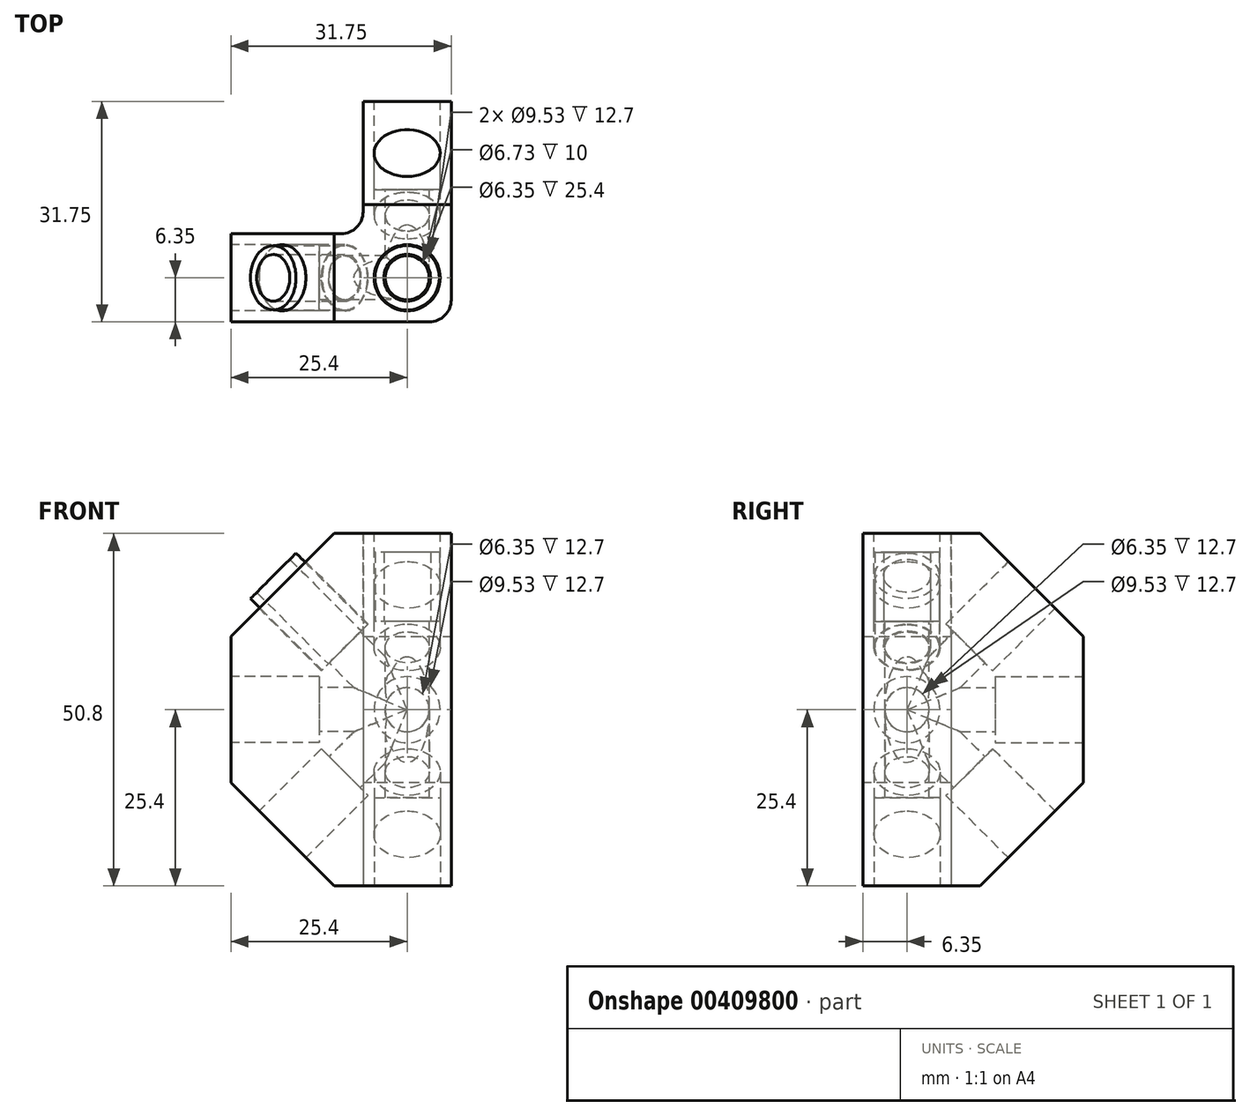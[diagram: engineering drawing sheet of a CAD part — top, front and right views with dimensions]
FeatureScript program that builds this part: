
annotation { "Feature Type Name" : "Feature", "Feature Type Description" : "" }
export const myFeature = defineFeature(function(context is Context, id is Id, definition is map)
    precondition{}
    {
        {
            var Q0;
            Q0=qCreatedBy(makeId("Top.planeOp"),FACE);
            var sketch = newSketch(context, id + "F0", { "sketchPlane" : qUnion([Q0])});
            skLineSegment(sketch, "E0.bottom", {"start": v(-6.35, 6.35) * mm, "end": v(-25.4, 6.35) * mm});
            skLineSegment(sketch, "E0.top", {"start": v(6.35, -6.35) * mm, "end": v(-25.4, -6.35) * mm});
            skLineSegment(sketch, "E0.right", {"start": v(-25.4, 6.35) * mm, "end": v(-25.4, -6.35) * mm});
            skLineSegment(sketch, "E1.top", {"start": v(-6.35, 25.4) * mm, "end": v(6.35, 25.4) * mm});
            skLineSegment(sketch, "E1.left", {"start": v(-6.35, 6.35) * mm, "end": v(-6.35, 25.4) * mm});
            skLineSegment(sketch, "E1.right", {"start": v(6.35, -6.35) * mm, "end": v(6.35, 25.4) * mm});
            skSolve(sketch);
        }
        {
            var Q0;
            Q0 = qSketchRegion(id + "F0", true);
            extrude(context, id + "F1", {"entities" : qUnion([Q0]), "depth" : 50.8 * mm, "symmetric" : true});
        }
        {
            var Q0;
            Q0=makeQuery(id+"F1.opExtrude","CAP_EDGE",EDGE,{"disambiguationData":[OSD([sQuery(id+"F0.wireOp",EDGE,"E0.right")])],"isStart":false});
            var Q1;
            Q1=makeQuery(id+"F1.opExtrude","CAP_EDGE",EDGE,{"disambiguationData":[OSD([sQuery(id+"F0.wireOp",EDGE,"E0.right")])],"isStart":true});
            var Q2;
            Q2=makeQuery(id+"F1.opExtrude","CAP_EDGE",EDGE,{"disambiguationData":[OSD([sQuery(id+"F0.wireOp",EDGE,"E1.top")])],"isStart":true});
            var Q3;
            Q3=makeQuery(id+"F1.opExtrude","CAP_EDGE",EDGE,{"disambiguationData":[OSD([sQuery(id+"F0.wireOp",EDGE,"E1.top")])],"isStart":false});
            chamfer(context, id + "F2", {"entities" : qUnion([Q0, Q1, Q2, Q3]), "width" : 14.86 * mm, "tangentPropagation" : true});
        }
        {
            var Q0;
            Q0=makeQuery(id+"F1.opExtrude","CAP_FACE",FACE,{"disambiguationData":[OSD([sQuery(id+"F0.wireOp",EDGE,"E0.bottom"),sQuery(id+"F0.wireOp",EDGE,"E0.top"),sQuery(id+"F0.wireOp",EDGE,"E0.right"),sQuery(id+"F0.wireOp",EDGE,"E1.top"),sQuery(id+"F0.wireOp",EDGE,"E1.left"),sQuery(id+"F0.wireOp",EDGE,"E1.right")])],"isStart":false});
            var sketch = newSketch(context, id + "F3", { "sketchPlane" : qUnion([Q0])});
            skCircle(sketch, "E2", {"center": v(0, 0) * mm, "radius": 3.18 * mm});
            skSolve(sketch);
        }
        {
            var Q0;
            Q0 = qSketchRegion(id + "F3", true);
            extrude(context, id + "F4", {"entities" : qUnion([Q0]), "operationType" : NewBodyOperationType.REMOVE, "endBound" : BoundingType.THROUGH_ALL, "oppositeDirection" : true, "depth" : 25.4 * mm});
        }
        {
            var Q0;
            Q0=makeQuery(id+"F1.opExtrude","SWEPT_FACE",FACE,{"disambiguationData":[OSD([sQuery(id+"F0.wireOp",EDGE,"E0.right")])]});
            var sketch = newSketch(context, id + "F5", { "sketchPlane" : qUnion([Q0])});
            skCircle(sketch, "E3", {"center": v(0, 0) * mm, "radius": 3.18 * mm});
            skSolve(sketch);
        }
        {
            var Q0;
            Q0 = qSketchRegion(id + "F5", true);
            extrude(context, id + "F6", {"entities" : qUnion([Q0]), "operationType" : NewBodyOperationType.REMOVE, "endBound" : BoundingType.UP_TO_NEXT, "oppositeDirection" : true, "depth" : 25.4 * mm});
        }
        {
            var Q0;
            Q0=makeQuery(id+"F1.opExtrude","SWEPT_FACE",FACE,{"disambiguationData":[OSD([sQuery(id+"F0.wireOp",EDGE,"E1.top")])]});
            var sketch = newSketch(context, id + "F7", { "sketchPlane" : qUnion([Q0])});
            skCircle(sketch, "E4", {"center": v(0, 0) * mm, "radius": 3.18 * mm});
            skSolve(sketch);
        }
        {
            var Q0;
            Q0 = qSketchRegion(id + "F7", true);
            extrude(context, id + "F8", {"entities" : qUnion([Q0]), "operationType" : NewBodyOperationType.REMOVE, "endBound" : BoundingType.UP_TO_NEXT, "oppositeDirection" : true, "depth" : 25.4 * mm});
        }
        {
            var Q0;
            {var subQ0=sQuery(id+"F0.wireOp",EDGE,"E1.top");Q0=makeQuery(id+"F2.opChamfer","BLEND_FACE",FACE,{"disambiguationData":[OSD([subQ0]),TDD([makeQuery(id+"F1.opExtrude","CAP_EDGE",EDGE,{"disambiguationData":[OSD([subQ0])],"isStart":false})])]});}
            var sketch = newSketch(context, id + "F9", { "sketchPlane" : qUnion([Q0])});
            skCircle(sketch, "E5", {"center": v(0, 0) * mm, "radius": 3.18 * mm});
            skSolve(sketch);
        }
        {
            var Q0;
            Q0 = qSketchRegion(id + "F9", true);
            extrude(context, id + "F10", {"entities" : qUnion([Q0]), "operationType" : NewBodyOperationType.REMOVE, "endBound" : BoundingType.UP_TO_NEXT, "oppositeDirection" : true, "depth" : 25.4 * mm});
        }
        {
            var Q0;
            {var subQ0=sQuery(id+"F0.wireOp",EDGE,"E0.right");Q0=makeQuery(id+"F2.opChamfer","BLEND_FACE",FACE,{"disambiguationData":[OSD([subQ0]),TDD([makeQuery(id+"F1.opExtrude","CAP_EDGE",EDGE,{"disambiguationData":[OSD([subQ0])],"isStart":false})])]});}
            var sketch = newSketch(context, id + "F11", { "sketchPlane" : qUnion([Q0])});
            skCircle(sketch, "E6", {"center": v(0, 0) * mm, "radius": 3.18 * mm});
            skSolve(sketch);
        }
        {
            var Q0;
            Q0 = qSketchRegion(id + "F11", true);
            extrude(context, id + "F12", {"entities" : qUnion([Q0]), "operationType" : NewBodyOperationType.REMOVE, "endBound" : BoundingType.UP_TO_NEXT, "oppositeDirection" : true, "depth" : 25.4 * mm});
        }
        {
            var Q0;
            {var subQ0=sQuery(id+"F0.wireOp",EDGE,"E1.top");Q0=makeQuery(id+"F2.opChamfer","BLEND_FACE",FACE,{"disambiguationData":[OSD([subQ0]),TDD([makeQuery(id+"F1.opExtrude","CAP_EDGE",EDGE,{"disambiguationData":[OSD([subQ0])],"isStart":true})])]});}
            var sketch = newSketch(context, id + "F13", { "sketchPlane" : qUnion([Q0])});
            skCircle(sketch, "E7", {"center": v(0, 0) * mm, "radius": 3.18 * mm});
            skSolve(sketch);
        }
        {
            var Q0;
            Q0 = qSketchRegion(id + "F13", true);
            extrude(context, id + "F14", {"entities" : qUnion([Q0]), "operationType" : NewBodyOperationType.REMOVE, "endBound" : BoundingType.UP_TO_NEXT, "oppositeDirection" : true, "depth" : 25.4 * mm});
        }
        {
            var Q0;
            {var subQ0=sQuery(id+"F0.wireOp",EDGE,"E0.right");Q0=makeQuery(id+"F2.opChamfer","BLEND_FACE",FACE,{"disambiguationData":[OSD([subQ0]),TDD([makeQuery(id+"F1.opExtrude","CAP_EDGE",EDGE,{"disambiguationData":[OSD([subQ0])],"isStart":true})])]});}
            var sketch = newSketch(context, id + "F15", { "sketchPlane" : qUnion([Q0])});
            skCircle(sketch, "E8", {"center": v(0, 0) * mm, "radius": 3.18 * mm});
            skSolve(sketch);
        }
        {
            var Q0;
            Q0 = qSketchRegion(id + "F15", true);
            extrude(context, id + "F16", {"entities" : qUnion([Q0]), "operationType" : NewBodyOperationType.REMOVE, "endBound" : BoundingType.UP_TO_NEXT, "oppositeDirection" : true, "depth" : 25.4 * mm});
        }
        {
            var Q0;
            Q0=makeQuery(id+"F1.opExtrude","SWEPT_EDGE",EDGE,{"disambiguationData":[OSD([sQuery(id+"F0.wireOp",EDGE,"E0.bottom"),sQuery(id+"F0.wireOp",EDGE,"E1.left")])]});
            fillet(context, id + "F17", {"entities" : qUnion([Q0]), "radius" : 3.17 * mm, "tangentPropagation" : true, "allowEdgeOverflow" : false});
        }
        {
            var Q0;
            Q0=makeQuery(id+"F1.opExtrude","SWEPT_EDGE",EDGE,{"disambiguationData":[OSD([sQuery(id+"F0.wireOp",EDGE,"E0.top"),sQuery(id+"F0.wireOp",EDGE,"E1.right")])]});
            fillet(context, id + "F18", {"entities" : qUnion([Q0]), "radius" : 3.17 * mm, "tangentPropagation" : true, "allowEdgeOverflow" : false});
        }
        {
            var Q0;
            Q0=makeQuery(id+"F1.opExtrude","CAP_FACE",FACE,{"disambiguationData":[OSD([sQuery(id+"F0.wireOp",EDGE,"E0.bottom"),sQuery(id+"F0.wireOp",EDGE,"E0.top"),sQuery(id+"F0.wireOp",EDGE,"E0.right"),sQuery(id+"F0.wireOp",EDGE,"E1.top"),sQuery(id+"F0.wireOp",EDGE,"E1.left"),sQuery(id+"F0.wireOp",EDGE,"E1.right")])],"isStart":true});
            var sketch = newSketch(context, id + "F19", { "sketchPlane" : qUnion([Q0])});
            skCircle(sketch, "E9", {"center": v(0, 0) * mm, "radius": 4.76 * mm});
            skSolve(sketch);
        }
        {
            var Q0;
            Q0 = qSketchRegion(id + "F19", true);
            extrude(context, id + "F20", {"entities" : qUnion([Q0]), "operationType" : NewBodyOperationType.REMOVE, "oppositeDirection" : true, "depth" : 12.7 * mm});
        }
        {
            var Q0;
            Q0=makeQuery(id+"F1.opExtrude","CAP_FACE",FACE,{"disambiguationData":[OSD([sQuery(id+"F0.wireOp",EDGE,"E0.bottom"),sQuery(id+"F0.wireOp",EDGE,"E0.top"),sQuery(id+"F0.wireOp",EDGE,"E0.right"),sQuery(id+"F0.wireOp",EDGE,"E1.top"),sQuery(id+"F0.wireOp",EDGE,"E1.left"),sQuery(id+"F0.wireOp",EDGE,"E1.right")])],"isStart":false});
            var sketch = newSketch(context, id + "F21", { "sketchPlane" : qUnion([Q0])});
            skCircle(sketch, "E10", {"center": v(0, 0) * mm, "radius": 4.76 * mm});
            skSolve(sketch);
        }
        {
            var Q0;
            Q0 = qSketchRegion(id + "F21", true);
            extrude(context, id + "F22", {"entities" : qUnion([Q0]), "operationType" : NewBodyOperationType.REMOVE, "oppositeDirection" : true, "depth" : 12.7 * mm});
        }
        {
            var Q0;
            Q0=makeQuery(id+"F1.opExtrude","SWEPT_FACE",FACE,{"disambiguationData":[OSD([sQuery(id+"F0.wireOp",EDGE,"E0.right")])]});
            var sketch = newSketch(context, id + "F23", { "sketchPlane" : qUnion([Q0])});
            skCircle(sketch, "E11", {"center": v(0, 0) * mm, "radius": 4.76 * mm});
            skSolve(sketch);
        }
        {
            var Q0;
            Q0 = qSketchRegion(id + "F23", true);
            extrude(context, id + "F24", {"entities" : qUnion([Q0]), "operationType" : NewBodyOperationType.REMOVE, "oppositeDirection" : true, "depth" : 12.7 * mm});
        }
        {
            var Q0;
            Q0=makeQuery(id+"F1.opExtrude","SWEPT_FACE",FACE,{"disambiguationData":[OSD([sQuery(id+"F0.wireOp",EDGE,"E1.top")])]});
            var sketch = newSketch(context, id + "F25", { "sketchPlane" : qUnion([Q0])});
            skCircle(sketch, "E12", {"center": v(0, 0) * mm, "radius": 4.76 * mm});
            skSolve(sketch);
        }
        {
            var Q0;
            Q0 = qSketchRegion(id + "F25", true);
            extrude(context, id + "F26", {"entities" : qUnion([Q0]), "operationType" : NewBodyOperationType.REMOVE, "oppositeDirection" : true, "depth" : 12.7 * mm});
        }
        {
            var Q0;
            {var subQ0=sQuery(id+"F0.wireOp",EDGE,"E0.right");Q0=makeQuery(id+"F2.opChamfer","BLEND_FACE",FACE,{"disambiguationData":[OSD([subQ0]),TDD([makeQuery(id+"F1.opExtrude","CAP_EDGE",EDGE,{"disambiguationData":[OSD([subQ0])],"isStart":false})])]});}
            var sketch = newSketch(context, id + "F27", { "sketchPlane" : qUnion([Q0])});
            skCircle(sketch, "E13", {"center": v(0, 0) * mm, "radius": 4.76 * mm});
            skSolve(sketch);
        }
        {
            var Q0;
            Q0 = qSketchRegion(id + "F27", true);
            extrude(context, id + "F28", {"entities" : qUnion([Q0]), "operationType" : NewBodyOperationType.REMOVE, "oppositeDirection" : true, "depth" : 12.7 * mm});
        }
        {
            var Q0;
            {var subQ0=sQuery(id+"F0.wireOp",EDGE,"E1.top");Q0=makeQuery(id+"F2.opChamfer","BLEND_FACE",FACE,{"disambiguationData":[OSD([subQ0]),TDD([makeQuery(id+"F1.opExtrude","CAP_EDGE",EDGE,{"disambiguationData":[OSD([subQ0])],"isStart":false})])]});}
            var sketch = newSketch(context, id + "F29", { "sketchPlane" : qUnion([Q0])});
            skCircle(sketch, "E14", {"center": v(0, 0) * mm, "radius": 4.76 * mm});
            skSolve(sketch);
        }
        {
            var Q0;
            Q0 = qSketchRegion(id + "F29", true);
            extrude(context, id + "F30", {"entities" : qUnion([Q0]), "operationType" : NewBodyOperationType.REMOVE, "oppositeDirection" : true, "depth" : 12.7 * mm});
        }
        {
            var Q0;
            {var subQ0=sQuery(id+"F0.wireOp",EDGE,"E1.top");Q0=makeQuery(id+"F2.opChamfer","BLEND_FACE",FACE,{"disambiguationData":[OSD([subQ0]),TDD([makeQuery(id+"F1.opExtrude","CAP_EDGE",EDGE,{"disambiguationData":[OSD([subQ0])],"isStart":true})])]});}
            var sketch = newSketch(context, id + "F31", { "sketchPlane" : qUnion([Q0])});
            skCircle(sketch, "E15", {"center": v(0, 0) * mm, "radius": 4.76 * mm});
            skSolve(sketch);
        }
        {
            var Q0;
            Q0 = qSketchRegion(id + "F31", true);
            extrude(context, id + "F32", {"entities" : qUnion([Q0]), "operationType" : NewBodyOperationType.REMOVE, "oppositeDirection" : true, "depth" : 12.7 * mm});
        }
        {
            var Q0;
            {var subQ0=sQuery(id+"F0.wireOp",EDGE,"E0.right");Q0=makeQuery(id+"F2.opChamfer","BLEND_FACE",FACE,{"disambiguationData":[OSD([subQ0]),TDD([makeQuery(id+"F1.opExtrude","CAP_EDGE",EDGE,{"disambiguationData":[OSD([subQ0])],"isStart":true})])]});}
            var sketch = newSketch(context, id + "F33", { "sketchPlane" : qUnion([Q0])});
            skCircle(sketch, "E16", {"center": v(0, 0) * mm, "radius": 4.76 * mm});
            skSolve(sketch);
        }
        {
            assignVariable(context, id + "F34", {"name" : "L1", "anyValue" : 10});
        }
        {
            assignVariable(context, id + "F35", {"name" : "L2", "anyValue" : (getVariable(context, 'L1') + 1.03) * 1.41 - 1.03});
        }
        {
            var Q0;
            Q0 = qSketchRegion(id + "F33", true);
            extrude(context, id + "F36", {"entities" : qUnion([Q0]), "operationType" : NewBodyOperationType.REMOVE, "oppositeDirection" : true, "depth" : 12.7 * mm});
        }
        {
            var Q0;
            Q0=makeQuery(id+"F22.boolean.opBoolean","COPY",FACE,{"derivedFrom":makeQuery(id+"F22.opExtrude","CAP_FACE",FACE,{"disambiguationData":[OSD([sQuery(id+"F21.wireOp",EDGE,"E10")])],"isStart":false})});
            var sketch = newSketch(context, id + "F37", { "sketchPlane" : qUnion([Q0])});
            skCircle(sketch, "E17", {"center": v(0, 0) * mm, "radius": 4.64 * mm});
            skCircle(sketch, "E18", {"center": v(0, 0) * mm, "radius": 3.37 * mm});
            skSolve(sketch);
        }
        {
            var Q0;
            Q0 = qSketchRegion(id + "F37", true);
            extrude(context, id + "F38", {"entities" : qUnion([Q0]), "depth" : (getVariable(context, 'L1')) * mm});
        }
        {
            var Q0;
            Q0=makeQuery(id+"F28.boolean.opBoolean","COPY",FACE,{"derivedFrom":makeQuery(id+"F28.opExtrude","CAP_FACE",FACE,{"disambiguationData":[OSD([sQuery(id+"F27.wireOp",EDGE,"E13")])],"isStart":false})});
            var sketch = newSketch(context, id + "F39", { "sketchPlane" : qUnion([Q0])});
            skCircle(sketch, "E19", {"center": v(0, 0) * mm, "radius": 4.64 * mm});
            skCircle(sketch, "E20", {"center": v(0, 0) * mm, "radius": 3.37 * mm});
            skSolve(sketch);
        }
        {
            var Q0;
            Q0 = qSketchRegion(id + "F39", true);
            extrude(context, id + "F40", {"entities" : qUnion([Q0]), "depth" : (getVariable(context, 'L2')) * mm});
        }
    });
